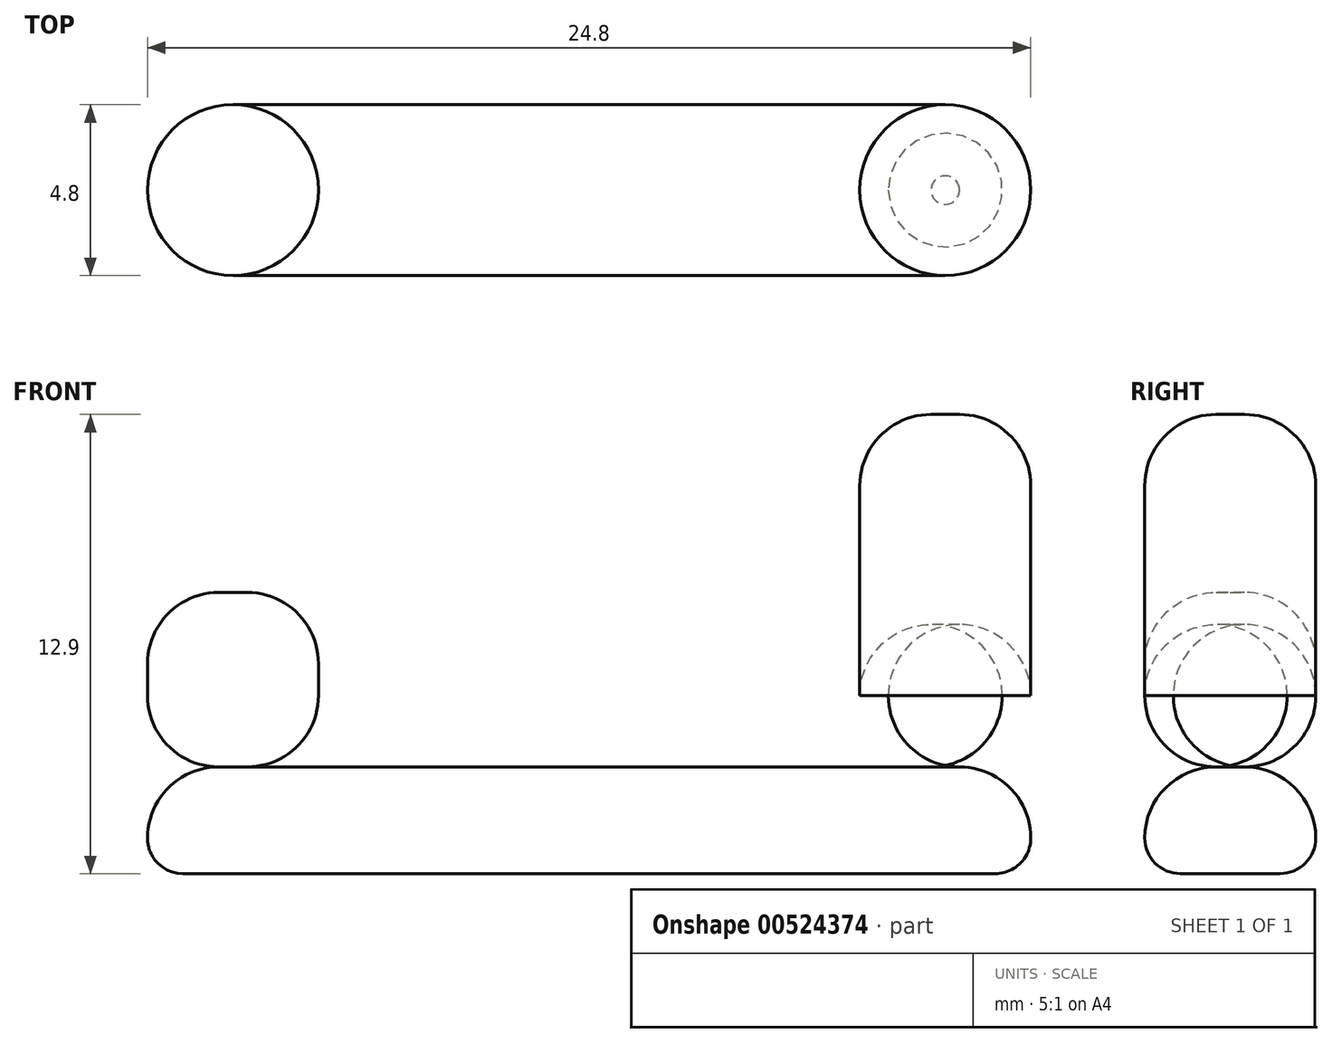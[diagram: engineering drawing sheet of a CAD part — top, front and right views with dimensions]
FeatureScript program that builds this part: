
annotation { "Feature Type Name" : "Feature", "Feature Type Description" : "" }
export const myFeature = defineFeature(function(context is Context, id is Id, definition is map)
    precondition{}
    {
        {
            var Q0;
            Q0=qCreatedBy(makeId("Top.planeOp"),FACE);
            var sketch = newSketch(context, id + "F0", { "sketchPlane" : qUnion([Q0])});
            skCircle(sketch, "E0", {"center": v(0, 0) * mm, "radius": 2.4 * mm});
            skSolve(sketch);
        }
        {
            var Q0;
            Q0 = qSketchRegion(id + "F0", true);
            extrude(context, id + "F1", {"entities" : qUnion([Q0]), "depth" : (7.4 + 5 - 2.5) * mm, "offsetDistance" : 25 * mm});
        }
        {
            var Q0;
            Q0=makeQuery(id+"F1.opExtrude","CAP_EDGE",EDGE,{"disambiguationData":[OSD([sQuery(id+"F0.wireOp",EDGE,"E0")])],"isStart":false});
            fillet(context, id + "F2", {"entities" : qUnion([Q0]), "radius" : 2 * mm, "tangentPropagation" : true, "allowEdgeOverflow" : false});
        }
        {
            var Q0;
            Q0=makeQuery(id+"F1.opExtrude","CAP_FACE",FACE,{"disambiguationData":[OSD([sQuery(id+"F0.wireOp",EDGE,"E0")])],"isStart":true});
            var sketch = newSketch(context, id + "F3", { "sketchPlane" : qUnion([Q0])});
            skCircle(sketch, "E1", {"center": v(-20, 0) * mm, "radius": 2.4 * mm});
            skSolve(sketch);
        }
        {
            var Q0;
            Q0=makeQuery(id+"F3.imprint","IMPRINT",FACE,{"disambiguationData":[TD([[makeQuery(id+"F3.imprint","IMPRINT",EDGE,{"derivedFrom":sQuery(id+"F3.wireOp",EDGE,"E1")}),1.0]])]});
            var Q1;
            Q1=makeQuery(id+"F1.opExtrude","CAP_FACE",FACE,{"disambiguationData":[OSD([sQuery(id+"F0.wireOp",EDGE,"E0")])],"isStart":false});
            extrude(context, id + "F4", {"entities" : qUnion([Q0]), "endBound" : BoundingType.UP_TO_SURFACE, "oppositeDirection" : true, "depth" : 25 * mm, "endBoundEntityFace" : qUnion([Q1]), "hasOffset" : true, "offsetDistance" : 5 * mm});
        }
        {
            var Q0;
            Q0=makeQuery(id+"F4.opExtrude","CAP_EDGE",EDGE,{"disambiguationData":[OSD([sQuery(id+"F3.wireOp",EDGE,"E1")])],"isStart":false});
            fillet(context, id + "F5", {"entities" : qUnion([Q0]), "radius" : 2 * mm, "tangentPropagation" : true, "allowEdgeOverflow" : false});
        }
        {
            var Q0;
            Q0=makeQuery(id+"F4.opExtrude","CAP_FACE",FACE,{"disambiguationData":[OSD([sQuery(id+"F3.wireOp",EDGE,"E1")])],"isStart":true});
            var sketch = newSketch(context, id + "F6", { "sketchPlane" : qUnion([Q0])});
            skArc(sketch, "E2.0", {"start": v(0, -2.4) * mm, "mid": v(2.4, 0) * mm, "end": v(0, 2.4) * mm});
            skLineSegment(sketch, "E3", {"start": v(-20, 2.4) * mm, "end": v(0, 2.4) * mm});
            skLineSegment(sketch, "E4", {"start": v(0, -2.4) * mm, "end": v(-20, -2.4) * mm});
            skArc(sketch, "E5.0", {"start": v(-20, 2.4) * mm, "mid": v(-22.4, 0) * mm, "end": v(-20, -2.4) * mm});
            skSolve(sketch);
        }
        {
            var Q0;
            Q0 = qSketchRegion(id + "F6", true);
            extrude(context, id + "F7", {"entities" : qUnion([Q0]), "depth" : 3 * mm, "offsetDistance" : 25 * mm});
        }
        {
            var Q0;
            Q0=makeQuery(id+"F7.opExtrude","CAP_EDGE",EDGE,{"disambiguationData":[OSD([sQuery(id+"F6.wireOp",EDGE,"E3")])],"isStart":false});
            fillet(context, id + "F8", {"entities" : qUnion([Q0]), "radius" : 1 * mm, "tangentPropagation" : true, "allowEdgeOverflow" : false});
        }
        {
            var Q0;
            Q0=makeQuery(id+"F4.opExtrude","CAP_EDGE",EDGE,{"disambiguationData":[OSD([sQuery(id+"F3.wireOp",EDGE,"E1")])],"isStart":true});
            var Q1;
            Q1=makeQuery(id+"F1.opExtrude","CAP_EDGE",EDGE,{"disambiguationData":[OSD([sQuery(id+"F0.wireOp",EDGE,"E0")])],"isStart":true});
            var Q2;
            Q2=makeQuery(id+"F7.opExtrude","CAP_EDGE",EDGE,{"disambiguationData":[OSD([sQuery(id+"F6.wireOp",EDGE,"E3")])],"isStart":true});
            var Q3;
            Q3=makeQuery(id+"F7.opExtrude","CAP_EDGE",EDGE,{"disambiguationData":[OSD([sQuery(id+"F6.wireOp",EDGE,"E4")])],"isStart":true});
            fillet(context, id + "F9", {"entities" : qUnion([Q0, Q1, Q2, Q3]), "radius" : 2 * mm, "tangentPropagation" : true, "allowEdgeOverflow" : false});
        }
    });
